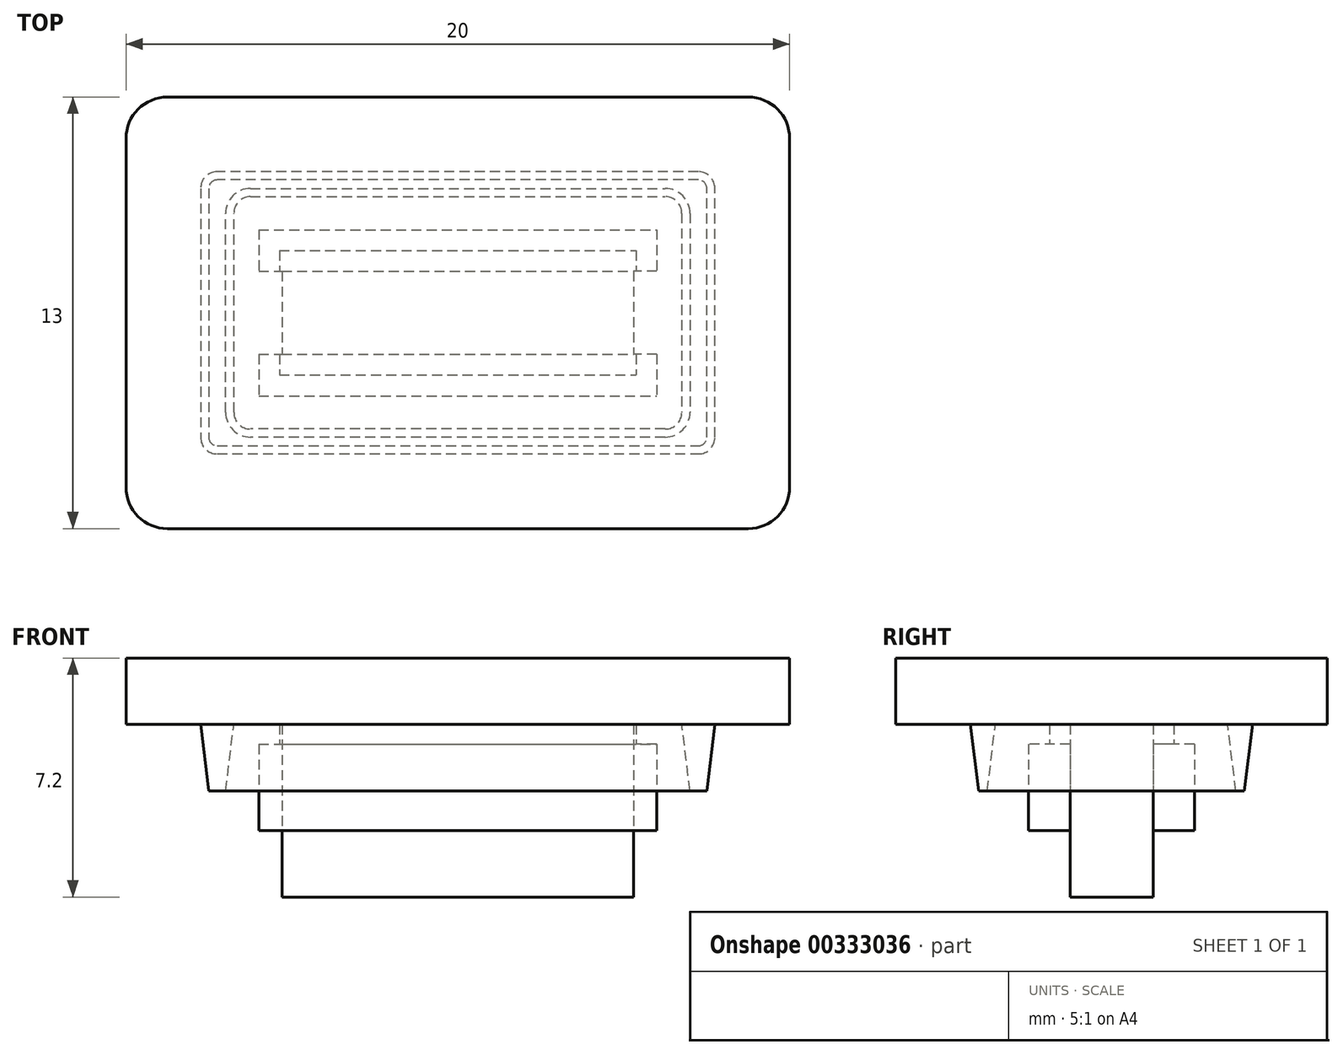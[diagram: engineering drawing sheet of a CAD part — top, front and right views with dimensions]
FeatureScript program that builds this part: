
annotation { "Feature Type Name" : "Feature", "Feature Type Description" : "" }
export const myFeature = defineFeature(function(context is Context, id is Id, definition is map)
    precondition{}
    {
        {
            var Q0;
            Q0=qCreatedBy(makeId("Top.planeOp"),FACE);
            var sketch = newSketch(context, id + "F0", { "sketchPlane" : qUnion([Q0])});
            skLineSegment(sketch, "E0.bottom", {"start": v(-6, 2.5) * mm, "end": v(6, 2.5) * mm});
            skLineSegment(sketch, "E0.top", {"start": v(-6, -2.5) * mm, "end": v(6, -2.5) * mm});
            skLineSegment(sketch, "E0.left", {"start": v(-6, 2.5) * mm, "end": v(-6, -2.5) * mm});
            skLineSegment(sketch, "E0.right", {"start": v(6, 2.5) * mm, "end": v(6, -2.5) * mm});
            skPoint(sketch, "E0.middle", {"position": v(0, 0) * mm});
            skLineSegment(sketch, "E1.bottom", {"start": v(-6, 1.25) * mm, "end": v(-5.3, 1.25) * mm});
            skLineSegment(sketch, "E1.top", {"start": v(-6, -1.25) * mm, "end": v(-5.3, -1.25) * mm});
            skLineSegment(sketch, "E1.left", {"start": v(-6, 1.25) * mm, "end": v(-6, -1.25) * mm});
            skLineSegment(sketch, "E1.right", {"start": v(-5.3, 1.25) * mm, "end": v(-5.3, -1.25) * mm});
            skLineSegment(sketch, "E2.MirrorCS", {"start": v(5.3, 1.25) * mm, "end": v(5.3, -1.25) * mm});
            skLineSegment(sketch, "E3.MirrorCS", {"start": v(6, 1.25) * mm, "end": v(6, -1.25) * mm});
            skLineSegment(sketch, "E4.MirrorCS", {"start": v(6, -1.25) * mm, "end": v(5.3, -1.25) * mm});
            skLineSegment(sketch, "E5.MirrorCS", {"start": v(6, 1.25) * mm, "end": v(5.3, 1.25) * mm});
            skSolve(sketch);
        }
        {
            var Q0;
            {var subQ6=sQuery(id+"F0.wireOp",EDGE,"E0.bottom");Q0=makeQuery(id+"F0.imprint","IMPRINT",FACE,{"disambiguationData":[TD([[makeQuery(id+"F0.imprint","IMPRINT",EDGE,{"derivedFrom":subQ6}),-1.0]])]});}
            extrude(context, id + "F1", {"entities" : qUnion([Q0]), "depth" : 2.6 * mm});
        }
        {
            var Q0;
            Q0=makeQuery(id+"F1.opExtrude","CAP_FACE",FACE,{"disambiguationData":[OSD([sQuery(id+"F0.wireOp",EDGE,"E0.bottom"),sQuery(id+"F0.wireOp",EDGE,"E0.top"),sQuery(id+"F0.wireOp",EDGE,"E0.left"),sQuery(id+"F0.wireOp",EDGE,"E0.right"),sQuery(id+"F0.wireOp",EDGE,"E1.bottom"),sQuery(id+"F0.wireOp",EDGE,"E1.top"),sQuery(id+"F0.wireOp",EDGE,"E1.right"),sQuery(id+"F0.wireOp",EDGE,"E2.MirrorCS"),sQuery(id+"F0.wireOp",EDGE,"E4.MirrorCS"),sQuery(id+"F0.wireOp",EDGE,"E5.MirrorCS")])],"isStart":true});
            var sketch = newSketch(context, id + "F2", { "sketchPlane" : qUnion([Q0])});
            skLineSegment(sketch, "E6.bottom", {"start": v(-5.3, 1.25) * mm, "end": v(5.3, 1.25) * mm});
            skLineSegment(sketch, "E6.top", {"start": v(-5.3, -1.25) * mm, "end": v(5.3, -1.25) * mm});
            skLineSegment(sketch, "E6.left", {"start": v(-5.3, 1.25) * mm, "end": v(-5.3, -1.25) * mm});
            skLineSegment(sketch, "E6.right", {"start": v(5.3, 1.25) * mm, "end": v(5.3, -1.25) * mm});
            skSolve(sketch);
        }
        {
            var Q0;
            Q0=qSketchRegion(id+"F2",true);
            extrude(context, id + "F3", {"entities" : qUnion([Q0]), "operationType" : NewBodyOperationType.ADD, "depth" : 2 * mm});
        }
        {
            var Q0;
            Q0=makeQuery(id+"F1.opExtrude","CAP_FACE",FACE,{"disambiguationData":[OSD([sQuery(id+"F0.wireOp",EDGE,"E0.bottom"),sQuery(id+"F0.wireOp",EDGE,"E0.top"),sQuery(id+"F0.wireOp",EDGE,"E0.left"),sQuery(id+"F0.wireOp",EDGE,"E0.right"),sQuery(id+"F0.wireOp",EDGE,"E1.bottom"),sQuery(id+"F0.wireOp",EDGE,"E1.top"),sQuery(id+"F0.wireOp",EDGE,"E1.right"),sQuery(id+"F0.wireOp",EDGE,"E2.MirrorCS"),sQuery(id+"F0.wireOp",EDGE,"E4.MirrorCS"),sQuery(id+"F0.wireOp",EDGE,"E5.MirrorCS")])],"isStart":false});
            var sketch = newSketch(context, id + "F4", { "sketchPlane" : qUnion([Q0])});
            skLineSegment(sketch, "E7.bottom", {"start": v(-5.37, 1.87) * mm, "end": v(5.37, 1.87) * mm});
            skLineSegment(sketch, "E7.top", {"start": v(-5.37, -1.87) * mm, "end": v(5.37, -1.87) * mm});
            skLineSegment(sketch, "E7.left", {"start": v(-5.37, 1.87) * mm, "end": v(-5.37, -1.87) * mm});
            skLineSegment(sketch, "E7.right", {"start": v(5.37, 1.87) * mm, "end": v(5.37, -1.87) * mm});
            skPoint(sketch, "E7.middle", {"position": v(0, 0) * mm});
            skSolve(sketch);
        }
        {
            var Q0;
            {var subQ15=sQuery(id+"F4.wireOp",EDGE,"ptJB8pNf-NBoq-jo5t-yNir-1qXlF4JjkNrf.bottom");Q0=makeQuery(id+"F4.imprint","IMPRINT",FACE,{"disambiguationData":[TD([[makeQuery(id+"F4.imprint","IMPRINT",EDGE,{"derivedFrom":subQ15}),-1.0]])]});}
            var Q1;
            {var subQ10=sQuery(id+"F4.wireOp",EDGE,"E7.bottom");Q1=makeQuery(id+"F4.imprint","IMPRINT",FACE,{"disambiguationData":[TD([[makeQuery(id+"F4.imprint","IMPRINT",EDGE,{"derivedFrom":subQ10}),-1.0]])]});}
            extrude(context, id + "F5", {"entities" : qUnion([Q0, Q1]), "operationType" : NewBodyOperationType.ADD, "depth" : .6 * mm});
        }
        {
            var Q0;
            Q0=makeQuery(id+"F5.opExtrude","CAP_FACE",FACE,{"disambiguationData":[OSD([sQuery(id+"F0.wireOp",EDGE,"E1.bottom"),sQuery(id+"F0.wireOp",EDGE,"E1.top"),sQuery(id+"F0.wireOp",EDGE,"E1.right"),sQuery(id+"F0.wireOp",EDGE,"E2.MirrorCS"),sQuery(id+"F0.wireOp",EDGE,"E4.MirrorCS"),sQuery(id+"F0.wireOp",EDGE,"E5.MirrorCS"),sQuery(id+"F4.wireOp",EDGE,"E7.bottom"),sQuery(id+"F4.wireOp",EDGE,"E7.top"),sQuery(id+"F4.wireOp",EDGE,"E7.left"),sQuery(id+"F4.wireOp",EDGE,"E7.right")])],"isStart":false});
            var sketch = newSketch(context, id + "F6", { "sketchPlane" : qUnion([Q0])});
            skLineSegment(sketch, "E8.bottom", {"start": v(-8.75, 6.5) * mm, "end": v(8.75, 6.5) * mm});
            skLineSegment(sketch, "E8.top", {"start": v(-8.75, -6.5) * mm, "end": v(8.75, -6.5) * mm});
            skLineSegment(sketch, "E8.left", {"start": v(-10, 5.25) * mm, "end": v(-10, -5.25) * mm});
            skLineSegment(sketch, "E8.right", {"start": v(10, 5.25) * mm, "end": v(10, -5.25) * mm});
            skPoint(sketch, "E8.middle", {"position": v(0, 0) * mm});
            skPoint(sketch, "E9.visualSharp", {"position": v(-10, -6.5) * mm});
            skArc(sketch, "E9.filletArc", {"start": v(-10, -5.25) * mm, "mid": v(-9.63, -6.13) * mm, "end": v(-8.75, -6.5) * mm});
            skPoint(sketch, "E10.visualSharp", {"position": v(10, -6.5) * mm});
            skArc(sketch, "E10.filletArc", {"start": v(8.75, -6.5) * mm, "mid": v(9.63, -6.13) * mm, "end": v(10, -5.25) * mm});
            skPoint(sketch, "E11.visualSharp", {"position": v(10, 6.5) * mm});
            skArc(sketch, "E11.filletArc", {"start": v(10, 5.25) * mm, "mid": v(9.63, 6.13) * mm, "end": v(8.75, 6.5) * mm});
            skPoint(sketch, "E12.visualSharp", {"position": v(-10, 6.5) * mm});
            skArc(sketch, "E12.filletArc", {"start": v(-8.75, 6.5) * mm, "mid": v(-9.63, 6.13) * mm, "end": v(-10, 5.25) * mm});
            skSolve(sketch);
        }
        {
            var Q0;
            Q0=qSketchRegion(id+"F6",true);
            extrude(context, id + "F7", {"entities" : qUnion([Q0]), "operationType" : NewBodyOperationType.ADD, "depth" : 2 * mm});
        }
        {
            var Q0;
            Q0=makeQuery(id+"F7.opExtrude","CAP_FACE",FACE,{"disambiguationData":[OSD([sQuery(id+"F6.wireOp",EDGE,"E8.bottom"),sQuery(id+"F6.wireOp",EDGE,"E8.top"),sQuery(id+"F6.wireOp",EDGE,"E8.left"),sQuery(id+"F6.wireOp",EDGE,"E8.right"),sQuery(id+"F6.wireOp",EDGE,"E9.filletArc"),sQuery(id+"F6.wireOp",EDGE,"E10.filletArc"),sQuery(id+"F6.wireOp",EDGE,"E11.filletArc"),sQuery(id+"F6.wireOp",EDGE,"E12.filletArc")])],"isStart":true});
            var sketch = newSketch(context, id + "F8", { "sketchPlane" : qUnion([Q0])});
            skLineSegment(sketch, "E13.bottom", {"start": v(-6.25, 3.5) * mm, "end": v(6.25, 3.5) * mm});
            skLineSegment(sketch, "E13.top", {"start": v(-6.25, -3.5) * mm, "end": v(6.25, -3.5) * mm});
            skLineSegment(sketch, "E13.left", {"start": v(-6.75, 3) * mm, "end": v(-6.75, -3) * mm});
            skLineSegment(sketch, "E13.right", {"start": v(6.75, 3) * mm, "end": v(6.75, -3) * mm});
            skPoint(sketch, "E13.middle", {"position": v(0, 0) * mm});
            skLineSegment(sketch, "E14.bottom", {"start": v(-7.25, 4.25) * mm, "end": v(7.25, 4.25) * mm});
            skLineSegment(sketch, "E14.top", {"start": v(-7.25, -4.25) * mm, "end": v(7.25, -4.25) * mm});
            skLineSegment(sketch, "E14.left", {"start": v(-7.75, 3.75) * mm, "end": v(-7.75, -3.75) * mm});
            skLineSegment(sketch, "E14.right", {"start": v(7.75, 3.75) * mm, "end": v(7.75, -3.75) * mm});
            skPoint(sketch, "E15.visualSharp", {"position": v(-6.75, 3.5) * mm});
            skArc(sketch, "E15.filletArc", {"start": v(-6.25, 3.5) * mm, "mid": v(-6.6, 3.35) * mm, "end": v(-6.75, 3) * mm});
            skPoint(sketch, "E16.visualSharp", {"position": v(6.75, 3.5) * mm});
            skArc(sketch, "E16.filletArc", {"start": v(6.75, 3) * mm, "mid": v(6.6, 3.35) * mm, "end": v(6.25, 3.5) * mm});
            skPoint(sketch, "E17.visualSharp", {"position": v(6.75, -3.5) * mm});
            skArc(sketch, "E17.filletArc", {"start": v(6.25, -3.5) * mm, "mid": v(6.6, -3.35) * mm, "end": v(6.75, -3) * mm});
            skPoint(sketch, "E18.visualSharp", {"position": v(-6.75, -3.5) * mm});
            skArc(sketch, "E18.filletArc", {"start": v(-6.75, -3) * mm, "mid": v(-6.6, -3.35) * mm, "end": v(-6.25, -3.5) * mm});
            skPoint(sketch, "E19.visualSharp", {"position": v(-7.75, 4.25) * mm});
            skArc(sketch, "E19.filletArc", {"start": v(-7.25, 4.25) * mm, "mid": v(-7.6, 4.1) * mm, "end": v(-7.75, 3.75) * mm});
            skPoint(sketch, "E20.visualSharp", {"position": v(7.75, 4.25) * mm});
            skArc(sketch, "E20.filletArc", {"start": v(7.75, 3.75) * mm, "mid": v(7.6, 4.1) * mm, "end": v(7.25, 4.25) * mm});
            skPoint(sketch, "E21.visualSharp", {"position": v(7.75, -4.25) * mm});
            skArc(sketch, "E21.filletArc", {"start": v(7.25, -4.25) * mm, "mid": v(7.6, -4.1) * mm, "end": v(7.75, -3.75) * mm});
            skPoint(sketch, "E22.visualSharp", {"position": v(-7.75, -4.25) * mm});
            skArc(sketch, "E22.filletArc", {"start": v(-7.75, -3.75) * mm, "mid": v(-7.6, -4.1) * mm, "end": v(-7.25, -4.25) * mm});
            skSolve(sketch);
        }
        {
            var Q0;
            Q0=qSketchRegion(id+"F8",true);
            extrude(context, id + "F9", {"entities" : qUnion([Q0]), "operationType" : NewBodyOperationType.ADD, "depth" : 2 * mm, "hasDraft" : true, "draftAngle" : 7 * degree, "draftPullDirection" : true});
        }
    });
